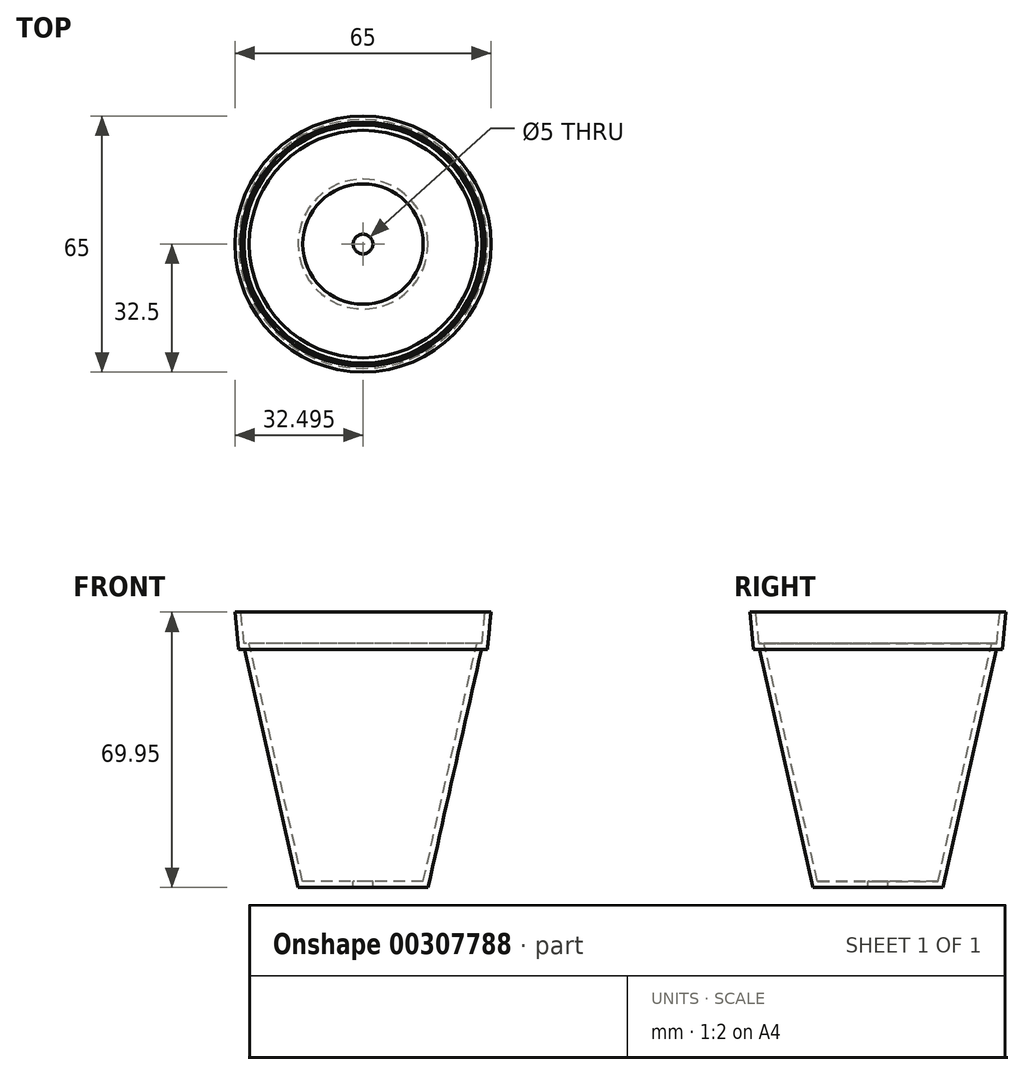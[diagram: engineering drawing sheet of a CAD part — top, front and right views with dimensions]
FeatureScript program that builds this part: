
annotation { "Feature Type Name" : "Feature", "Feature Type Description" : "" }
export const myFeature = defineFeature(function(context is Context, id is Id, definition is map)
    precondition{}
    {
        {
            var Q0;
            Q0=qCreatedBy(makeId("Front.planeOp"),FACE);
            var sketch = newSketch(context, id + "F0", { "sketchPlane" : qUnion([Q0])});
            skLineSegment(sketch, "E0", {"start": v(-22.98, -36.32) * mm, "end": v(-6.48, -36.32) * mm});
            skLineSegment(sketch, "E1", {"start": v(-22.98, 33.68) * mm, "end": v(-22.98, -36.32) * mm});
            skLineSegment(sketch, "E2", {"start": v(-6.48, -36.32) * mm, "end": v(7.13, 24.16) * mm});
            skLineSegment(sketch, "E3", {"start": v(7.13, 24.16) * mm, "end": v(8.63, 24.16) * mm});
            skLineSegment(sketch, "E4", {"start": v(9.52, 33.62) * mm, "end": v(-22.98, 33.68) * mm});
            skLineSegment(sketch, "E5", {"start": v(9.52, 33.62) * mm, "end": v(8.63, 24.16) * mm});
            skSolve(sketch);
        }
        {
            var Q0;
            Q0=makeQuery(id+"F0.imprint","IMPRINT",FACE,{"disambiguationData":[TD([[makeQuery(id+"F0.imprint","IMPRINT",EDGE,{"derivedFrom":sQuery(id+"F0.wireOp",EDGE,"E0")}),1.0]])]});
            var Q1;
            Q1=sQuery(id+"F0.wireOp",EDGE,"E1");
            revolve(context, id + "F1", {"entities" : qUnion([Q0]), "axis" : qUnion([Q1]), "revolveType" : RevolveType.FULL});
        }
        {
            var Q0;
            Q0=makeQuery(id+"F1.opRevolve","SWEPT_FACE",FACE,{"disambiguationData":[OSD([sQuery(id+"F0.wireOp",EDGE,"E4")])]});
            shell(context, id + "F2", {"entities" : qUnion([Q0]), "thickness" : 1.5 * mm});
        }
        {
            var Q0;
            Q0=makeQuery(id+"F1.opRevolve","SWEPT_FACE",FACE,{"disambiguationData":[OSD([sQuery(id+"F0.wireOp",EDGE,"E0")])]});
            var sketch = newSketch(context, id + "F3", { "sketchPlane" : qUnion([Q0])});
            skPoint(sketch, "E6", {"position": v(-22.98, 0) * mm});
            skSolve(sketch);
        }
        {
            var Q0;
            Q0=sQuery(id+"F3.wireOp",VERTEX,"E6");
            var Q1;
            Q1=makeQuery(id+"F1.opRevolve","SWEPT_BODY",BODY,{"disambiguationData":[OSD([sQuery(id+"F0.wireOp",EDGE,"E0"),sQuery(id+"F0.wireOp",EDGE,"E1"),sQuery(id+"F0.wireOp",EDGE,"E2"),sQuery(id+"F0.wireOp",EDGE,"E3"),sQuery(id+"F0.wireOp",EDGE,"E4"),sQuery(id+"F0.wireOp",EDGE,"E5")])]});
            hole(context, id + "F4", {"style" : HoleStyle.SIMPLE, "endStyle" : HoleEndStyle.THROUGH, "holeDiameter" : 5 * mm, "tappedDepth" : 12 * mm, "tapClearance" : 3, "locations" : qUnion([Q0]), "scope" : qUnion([Q1])});
        }
    });
